# Revit family: MI-HUB-ARC-CL
name_source: partatom
category: Pipe Accessories
units: mm (PartAtom-declared; Revit-internal decimal feet)

## family parameters
Always vertical = No
Cut with Voids When Loaded = No
Part Type = Normal
Round Connector Dimension = Use Diameter
Shared = No
Work Plane-Based = No

## types (6) — shared parameters
Default Elevation = 0.00"
Description = SHIELDED REPAIR COUPLINGS - CLAY TO CAST IRON, PLASTIC, LEAD OR STEEL
Manufacturer = MIFAB
URL = WWW.MIFAB.COM

## per-type parameters (varying)
| type | Coupling height | Coupling inner width | Coupling outer width |
| MI-HUB-ARC-CL-400 | 4.07" | 4.51" | 5.36" |
| MI-HUB-ARC-CL-500 | 5.74" | 5.50" | 6.60" |
| MI-HUB-ARC-CL-600 | 5.89" | 6.56" | 7.50" |
| MI-HUB-ARC-CL-640 | 6.02" | 4.50" | 7.50" |
| MI-HUB-ARC-CL-860 | 6.00" | 6.63" | 9.65" |
| MI-HUB-ARC-CL-880 | 5.96" | 8.57" | 9.76" |

note: column(s) folded — value = type name in every type: Model

## geometry (parser evidence)
native form markers: Blend x4, Sweep x7
no freeform markers — native parametric forms only
